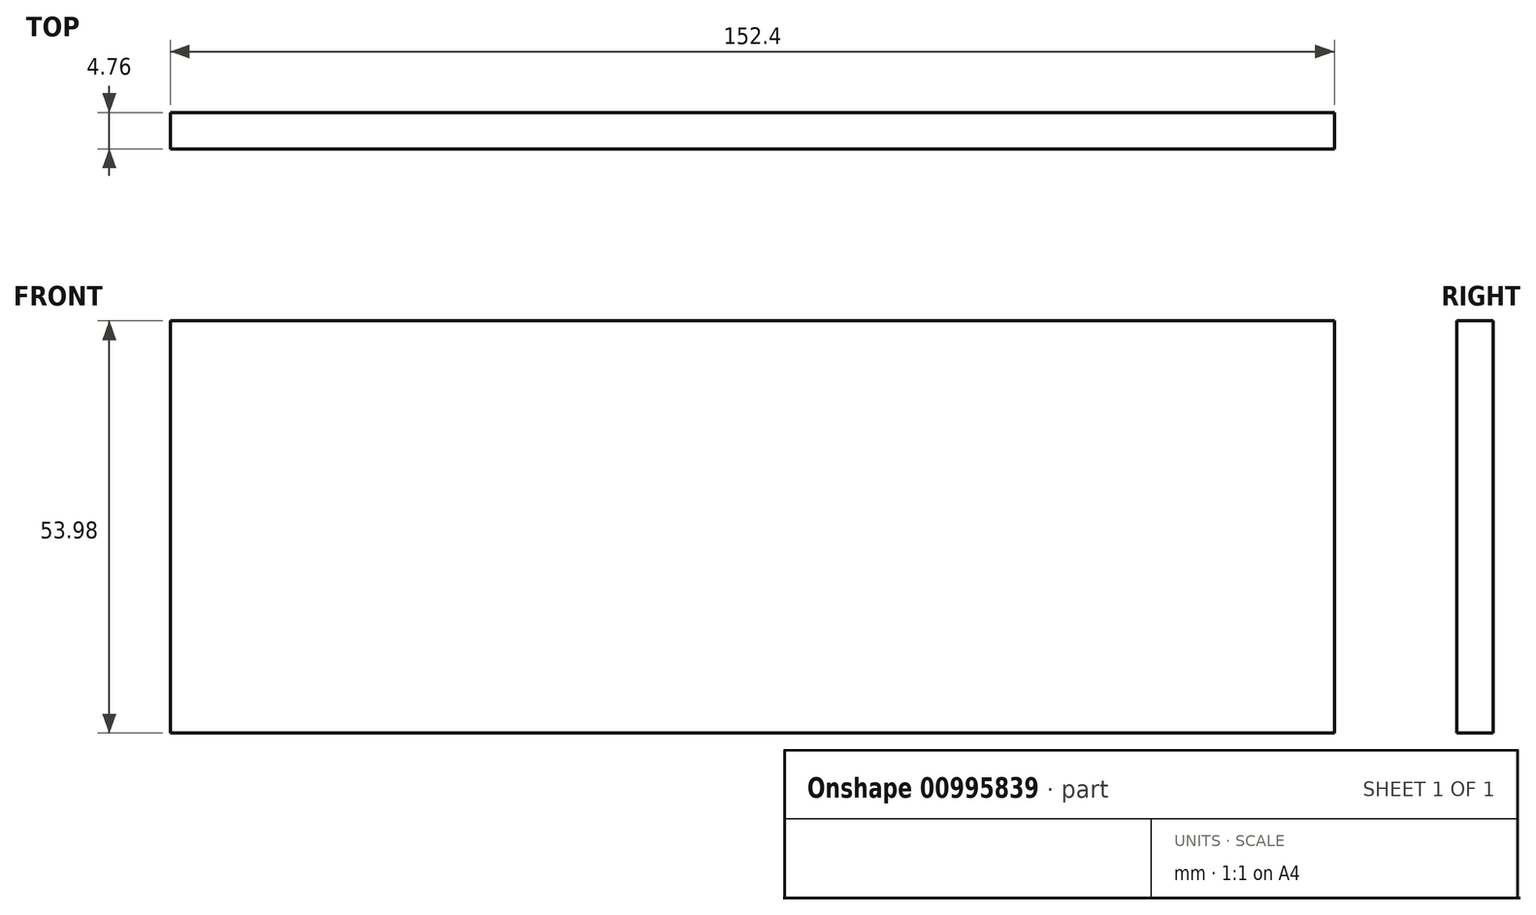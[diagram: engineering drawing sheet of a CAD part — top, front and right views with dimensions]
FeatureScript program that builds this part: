
annotation { "Feature Type Name" : "Feature", "Feature Type Description" : "" }
export const myFeature = defineFeature(function(context is Context, id is Id, definition is map)
    precondition{}
    {
        {
            var Q0;
            Q0=qCreatedBy(makeId("Front.planeOp"),FACE);
            var sketch = newSketch(context, id + "F0", { "sketchPlane" : qUnion([Q0])});
            skLineSegment(sketch, "E0.bottom", {"start": v(76.2, 26.99) * mm, "end": v(-76.2, 26.99) * mm});
            skLineSegment(sketch, "E0.top", {"start": v(76.2, -26.99) * mm, "end": v(-76.2, -26.99) * mm});
            skLineSegment(sketch, "E0.left", {"start": v(76.2, 26.99) * mm, "end": v(76.2, -26.99) * mm});
            skLineSegment(sketch, "E0.right", {"start": v(-76.2, 26.99) * mm, "end": v(-76.2, -26.99) * mm});
            skPoint(sketch, "E0.middle", {"position": v(0, 0) * mm});
            skSolve(sketch);
        }
        {
            var Q0;
            Q0 = qSketchRegion(id + "F0", true);
            extrude(context, id + "F1", {"entities" : qUnion([Q0]), "depth" : 4.76 * mm, "offsetDistance" : 25.4 * mm, "symmetric" : true});
        }
    });
